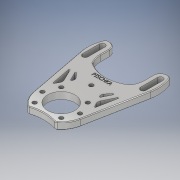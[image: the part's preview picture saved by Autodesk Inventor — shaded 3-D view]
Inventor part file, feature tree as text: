
AUTODESK INVENTOR PART (.ipt)
format: ipt  version: 2019.3 (Build 233278000, 278)  size: 681,472 bytes
history: native  units: mm
features: thread x7, emboss x2, fillet x2, sketch x2, extrude x1, chamfer x1, other x1
ambient origin geometry x8: Origin, YZ Plane, XZ Plane, XY Plane, X Axis, Y Axis, Z Axis, Center Point
bodies: Body1 (feature_tree)
feature tree (16):
  extrude  "Extrusion3"  Depth=20.0mm
  thread  "Thread1"  [1 undecoded]
  thread  "Thread2"  [1 undecoded]
  thread  "Thread3"  [1 undecoded]
  thread  "Thread4"  [1 undecoded]
  thread  "Thread5"  [1 undecoded]
  thread  "Thread6"  [1 undecoded]
  thread  "Thread7"  [1 undecoded]
  emboss  "Emboss1"
  emboss  "Emboss2"
  fillet  "Fillet3"  Radius=3.0mm
  fillet  "Fillet5"  Radius=3.0mm
  chamfer  "Chamfer3"  Distance=3.0mm
  other  "Center Lines"
  sketch  "Sketch1"  dims[d0=45.0mm d1=20.0mm d3=3.5mm d4=3.5mm d5=7.0mm d7=43.0mm d9=3.5mm d11=32.0mm d15=4.0mm d24=3.0mm d25=3.0mm]
  sketch  "Sketch3"  dims[d27=45.0deg d29=3.0mm d30=3.0mm d31=22.0mm d40=5.0mm d41=0.0mm d44=10.0mm d45=0.0mm d46=10.0mm d47=0.0mm d48=10.0mm d49=0.0mm d50=20.0mm d51=52.0mm d53=26.0mm d54=10.0mm d55=0.0mm d56=10.0mm d57=0.0mm d58=10.0mm d59=0.0mm d60=10.0mm d61=0.0mm d65=0.2mm d66=0.0mm d69=5.0mm d70=15.0mm d71=5.0mm d72=15.0mm d73=0.2mm d74=0.0mm d75=73.963203mm d76=7.5mm d77=3.75mm d78=1.0mm d81=6.25mm d82=12.5mm d85=4.0mm d86=3.0mm d91=0.5mm d94=2.0mm d95=0.5mm d96=2.0mm d97=45.0deg d98=15.0deg d99=24.0mm]
note: 7 required parameter values undecoded (feature->parameter linkage not recoverable at this tier; creation-order binding heuristic only, values carry confidence <= 0.55)
